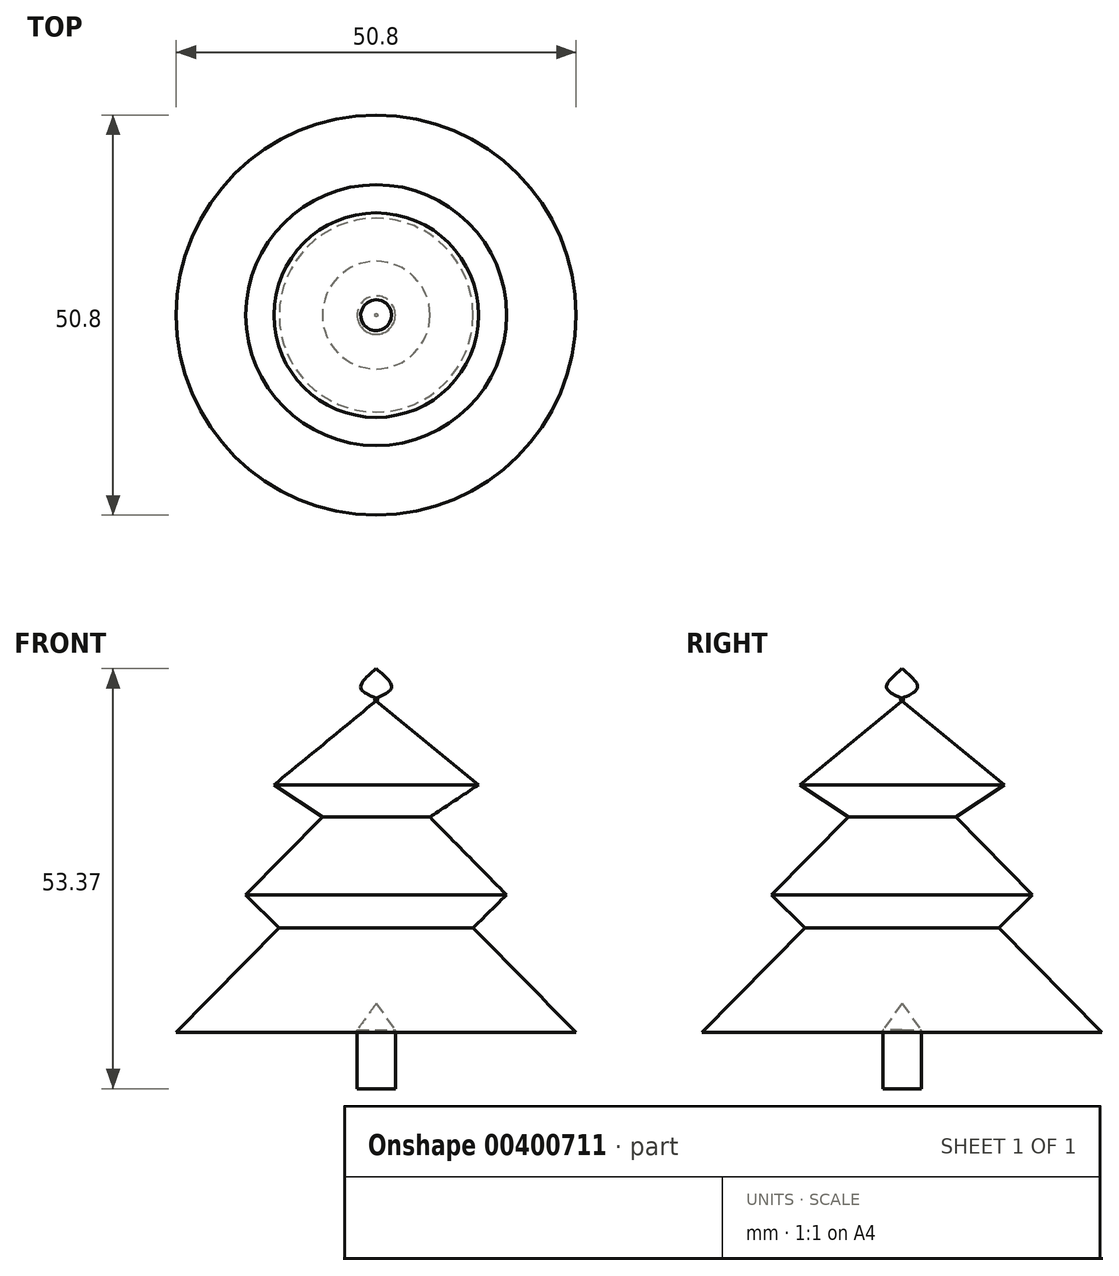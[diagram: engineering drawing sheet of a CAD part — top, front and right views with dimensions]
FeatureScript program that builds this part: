
annotation { "Feature Type Name" : "Feature", "Feature Type Description" : "" }
export const myFeature = defineFeature(function(context is Context, id is Id, definition is map)
    precondition{}
    {
        {
            var Q0;
            Q0=qCreatedBy(makeId("Right.planeOp"),FACE);
            var sketch = newSketch(context, id + "F0", { "sketchPlane" : qUnion([Q0])});
            skLineSegment(sketch, "E0", {"start": v(0, 47.68) * mm, "end": v(0, 5.56) * mm});
            skLineSegment(sketch, "E1", {"start": v(0, 47.68) * mm, "end": v(12.99, 37.02) * mm});
            skLineSegment(sketch, "E2", {"start": v(12.99, 37.02) * mm, "end": v(6.83, 32.92) * mm});
            skLineSegment(sketch, "E3", {"start": v(6.83, 32.92) * mm, "end": v(16.57, 23.04) * mm});
            skLineSegment(sketch, "E4", {"start": v(16.57, 23.04) * mm, "end": v(12.3, 18.85) * mm});
            skLineSegment(sketch, "E5", {"start": v(12.3, 18.85) * mm, "end": v(25.4, 5.56) * mm});
            skLineSegment(sketch, "E6", {"start": v(25.4, 5.56) * mm, "end": v(0, 5.56) * mm});
            skSolve(sketch);
        }
        {
            var Q0;
            Q0=makeQuery(id+"F0.imprint","IMPRINT",FACE,{"disambiguationData":[TD([[makeQuery(id+"F0.imprint","IMPRINT",EDGE,{"derivedFrom":sQuery(id+"F0.wireOp",EDGE,"E0")}),1.0]])]});
            var Q1;
            Q1=sQuery(id+"F0.wireOp",EDGE,"E0");
            revolve(context, id + "F1", {"entities" : qUnion([Q0]), "axis" : qUnion([Q1]), "revolveType" : RevolveType.FULL});
        }
        {
            var Q0;
            Q0=qCreatedBy(makeId("Front.planeOp"),FACE);
            var sketch = newSketch(context, id + "F2", { "sketchPlane" : qUnion([Q0])});
            skLineSegment(sketch, "E7", {"start": v(0, 48) * mm, "end": v(0, 51.79) * mm});
            skFitSpline(sketch, "E8", {"points": [v(0, 51.79) * mm, v(1.96, 49.4) * mm, v(0, 48) * mm], "startDerivative": vector(5.77, -4.9) * mm, "endDerivative": vector(-6.02, -2.62) * mm});
            skSolve(sketch);
        }
        {
            var Q0;
            Q0=makeQuery(id+"F2.imprint","IMPRINT",FACE,{"disambiguationData":[TD([[makeQuery(id+"F2.imprint","IMPRINT",EDGE,{"derivedFrom":sQuery(id+"F2.wireOp",EDGE,"E7")}),-1.0]])]});
            var Q1;
            Q1=sQuery(id+"F2.wireOp",EDGE,"E7");
            revolve(context, id + "F3", {"entities" : qUnion([Q0]), "axis" : qUnion([Q1]), "revolveType" : RevolveType.FULL});
        }
        {
            var Q0;
            Q0=qCreatedBy(makeId("Front.planeOp"),FACE);
            var sketch = newSketch(context, id + "F4", { "sketchPlane" : qUnion([Q0])});
            skLineSegment(sketch, "E9", {"start": v(0, 48.07) * mm, "end": v(0, 47.6) * mm});
            skPoint(sketch, "E10.1.internal.snap0", {"position": v(0, 47.83) * mm});
            skFitSpline(sketch, "E10", {"points": [v(0, 48.07) * mm, v(0.19, 47.83) * mm, v(0, 47.6) * mm], "startDerivative": vector(0.56, -0.48) * mm, "endDerivative": vector(-0.56, -0.48) * mm});
            skSolve(sketch);
        }
        {
            var Q0;
            Q0=makeQuery(id+"F4.imprint","IMPRINT",FACE,{"disambiguationData":[TD([[makeQuery(id+"F4.imprint","IMPRINT",EDGE,{"derivedFrom":sQuery(id+"F4.wireOp",EDGE,"E9")}),1.0]])]});
            var Q1;
            Q1=sQuery(id+"F4.wireOp",EDGE,"E9");
            revolve(context, id + "F5", {"entities" : qUnion([Q0]), "axis" : qUnion([Q1]), "revolveType" : RevolveType.FULL});
        }
        {
            var Q0;
            Q0=qCreatedBy(makeId("Right.planeOp"),FACE);
            var sketch = newSketch(context, id + "F6", { "sketchPlane" : qUnion([Q0])});
            skLineSegment(sketch, "E11", {"start": v(0, 9.24) * mm, "end": v(0, -1.58) * mm});
            skLineSegment(sketch, "E12", {"start": v(0, -1.58) * mm, "end": v(-2.44, -1.58) * mm});
            skLineSegment(sketch, "E13", {"start": v(-2.44, -1.58) * mm, "end": v(-2.44, 5.87) * mm});
            skLineSegment(sketch, "E14", {"start": v(-2.44, 5.87) * mm, "end": v(0, 9.24) * mm});
            skSolve(sketch);
        }
        {
            var Q0;
            Q0=makeQuery(id+"F6.imprint","IMPRINT",FACE,{"disambiguationData":[TD([[makeQuery(id+"F6.imprint","IMPRINT",EDGE,{"derivedFrom":sQuery(id+"F6.wireOp",EDGE,"E11")}),-1.0]])]});
            var Q1;
            Q1=sQuery(id+"F6.wireOp",EDGE,"E11");
            revolve(context, id + "F7", {"entities" : qUnion([Q0]), "axis" : qUnion([Q1]), "revolveType" : RevolveType.FULL});
        }
    });
